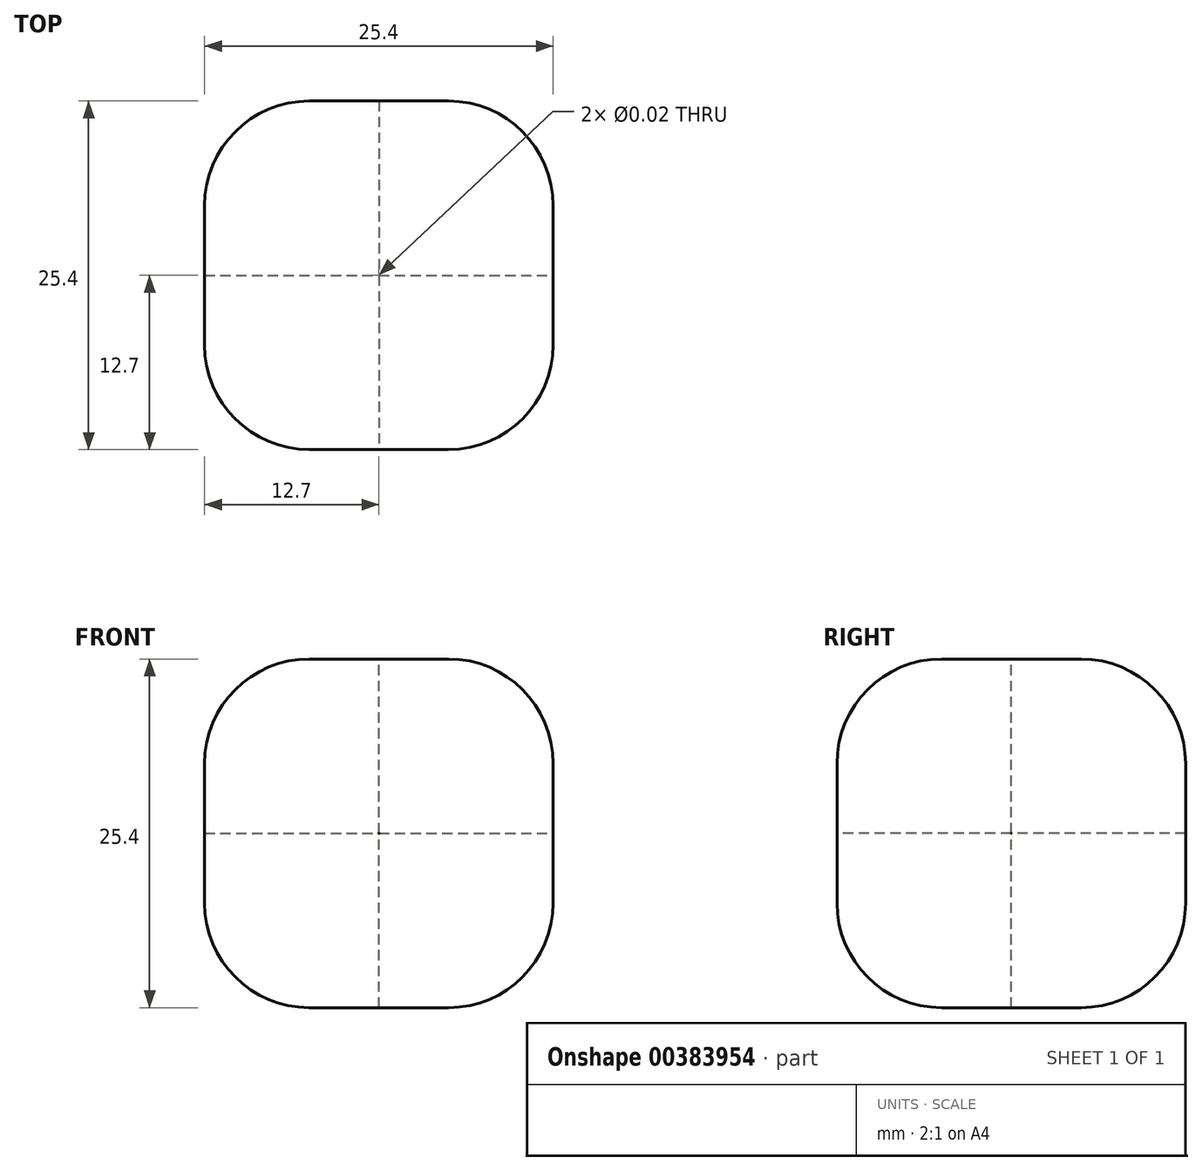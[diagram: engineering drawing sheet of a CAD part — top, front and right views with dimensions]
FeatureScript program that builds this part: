
annotation { "Feature Type Name" : "Feature", "Feature Type Description" : "" }
export const myFeature = defineFeature(function(context is Context, id is Id, definition is map)
    precondition{}
    {
        {
            var Q0;
            Q0=qCreatedBy(makeId("Front.planeOp"),FACE);
            var sketch = newSketch(context, id + "F0", { "sketchPlane" : qUnion([Q0])});
            skLineSegment(sketch, "E0.bottom", {"start": v(12.7, 12.7) * mm, "end": v(-12.7, 12.7) * mm});
            skLineSegment(sketch, "E0.top", {"start": v(12.7, -12.7) * mm, "end": v(-12.7, -12.7) * mm});
            skLineSegment(sketch, "E0.left", {"start": v(12.7, 12.7) * mm, "end": v(12.7, -12.7) * mm});
            skLineSegment(sketch, "E0.right", {"start": v(-12.7, 12.7) * mm, "end": v(-12.7, -12.7) * mm});
            skPoint(sketch, "E0.middle", {"position": v(0, 0) * mm});
            skSolve(sketch);
        }
        {
            var Q0;
            Q0 = qSketchRegion(id + "F0", true);
            extrude(context, id + "F1", {"entities" : qUnion([Q0]), "endBound" : BoundingType.SYMMETRIC, "depth" : 25.4 * mm});
        }
        {
            var Q0;
            Q0=makeQuery(id+"F1.opExtrude","SWEPT_FACE",FACE,{"disambiguationData":[OSD([sQuery(id+"F0.wireOp",EDGE,"E0.left")])]});
            var sketch = newSketch(context, id + "F2", { "sketchPlane" : qUnion([Q0])});
            skPoint(sketch, "E1", {"position": v(0, 0) * mm});
            skSolve(sketch);
        }
        {
            var Q0;
            Q0=makeQuery(id+"F1.opExtrude","CAP_FACE",FACE,{"disambiguationData":[OSD([sQuery(id+"F0.wireOp",EDGE,"E0.bottom"),sQuery(id+"F0.wireOp",EDGE,"E0.top"),sQuery(id+"F0.wireOp",EDGE,"E0.left"),sQuery(id+"F0.wireOp",EDGE,"E0.right")])],"isStart":false});
            var sketch = newSketch(context, id + "F3", { "sketchPlane" : qUnion([Q0])});
            skPoint(sketch, "E2", {"position": v(0, 0) * mm});
            skSolve(sketch);
        }
        {
            var Q0;
            Q0=makeQuery(id+"F1.opExtrude","SWEPT_FACE",FACE,{"disambiguationData":[OSD([sQuery(id+"F0.wireOp",EDGE,"E0.bottom")])]});
            var sketch = newSketch(context, id + "F4", { "sketchPlane" : qUnion([Q0])});
            skPoint(sketch, "E3", {"position": v(0, 0) * mm});
            skSolve(sketch);
        }
        {
            var Q0;
            Q0=sQuery(id+"F4.wireOp",VERTEX,"E3");
            var Q1;
            Q1=sQuery(id+"F3.wireOp",VERTEX,"E2");
            var Q2;
            Q2=sQuery(id+"F2.wireOp",VERTEX,"E1");
            var Q3;
            Q3=makeQuery(id+"F1.opExtrude","SWEPT_BODY",BODY,{"disambiguationData":[OSD([sQuery(id+"F0.wireOp",EDGE,"E0.bottom"),sQuery(id+"F0.wireOp",EDGE,"E0.top"),sQuery(id+"F0.wireOp",EDGE,"E0.left"),sQuery(id+"F0.wireOp",EDGE,"E0.right")])]});
            hole(context, id + "F5", {"style" : HoleStyle.SIMPLE, "endStyle" : HoleEndStyle.THROUGH, "standardTappedOrClearance" : lookupTablePath({ "standard" : "ANSI", "size" : "9/16 (0.56)", "type" : "Drilled" }), "standardBlindInLast" : lookupTablePath({ "standard" : "ANSI", "size" : "9/16", "type" : "Drilled" }), "holeDiameter" : 9 / 406.4 * mm, "isTappedThrough" : true, "tappedDepth" : 12.7 * mm, "tapClearance" : 3, "locations" : qUnion([Q0, Q1, Q2]), "scope" : qUnion([Q3])});
        }
        {
            var Q0;
            Q0=makeQuery(id+"F1.opExtrude","SWEPT_EDGE",EDGE,{"disambiguationData":[OSD([sQuery(id+"F0.wireOp",EDGE,"E0.bottom"),sQuery(id+"F0.wireOp",EDGE,"E0.left")])]});
            var Q1;
            Q1=makeQuery(id+"F1.opExtrude","SWEPT_EDGE",EDGE,{"disambiguationData":[OSD([sQuery(id+"F0.wireOp",EDGE,"E0.top"),sQuery(id+"F0.wireOp",EDGE,"E0.left")])]});
            var Q2;
            Q2=makeQuery(id+"F1.opExtrude","CAP_EDGE",EDGE,{"disambiguationData":[OSD([sQuery(id+"F0.wireOp",EDGE,"E0.left")])],"isStart":true});
            var Q3;
            Q3=makeQuery(id+"F1.opExtrude","CAP_EDGE",EDGE,{"disambiguationData":[OSD([sQuery(id+"F0.wireOp",EDGE,"E0.left")])],"isStart":false});
            var Q4;
            Q4=makeQuery(id+"F1.opExtrude","CAP_EDGE",EDGE,{"disambiguationData":[OSD([sQuery(id+"F0.wireOp",EDGE,"E0.bottom")])],"isStart":false});
            var Q5;
            Q5=makeQuery(id+"F1.opExtrude","CAP_EDGE",EDGE,{"disambiguationData":[OSD([sQuery(id+"F0.wireOp",EDGE,"E0.right")])],"isStart":false});
            var Q6;
            Q6=makeQuery(id+"F1.opExtrude","CAP_EDGE",EDGE,{"disambiguationData":[OSD([sQuery(id+"F0.wireOp",EDGE,"E0.top")])],"isStart":false});
            var Q7;
            Q7=makeQuery(id+"F1.opExtrude","SWEPT_EDGE",EDGE,{"disambiguationData":[OSD([sQuery(id+"F0.wireOp",EDGE,"E0.bottom"),sQuery(id+"F0.wireOp",EDGE,"E0.right")])]});
            var Q8;
            Q8=makeQuery(id+"F1.opExtrude","CAP_EDGE",EDGE,{"disambiguationData":[OSD([sQuery(id+"F0.wireOp",EDGE,"E0.bottom")])],"isStart":true});
            var Q9;
            Q9=makeQuery(id+"F1.opExtrude","SWEPT_EDGE",EDGE,{"disambiguationData":[OSD([sQuery(id+"F0.wireOp",EDGE,"E0.top"),sQuery(id+"F0.wireOp",EDGE,"E0.right")])]});
            var Q10;
            Q10=makeQuery(id+"F1.opExtrude","CAP_EDGE",EDGE,{"disambiguationData":[OSD([sQuery(id+"F0.wireOp",EDGE,"E0.right")])],"isStart":true});
            var Q11;
            Q11=makeQuery(id+"F1.opExtrude","CAP_EDGE",EDGE,{"disambiguationData":[OSD([sQuery(id+"F0.wireOp",EDGE,"E0.top")])],"isStart":true});
            fillet(context, id + "F6", {"entities" : qUnion([Q0, Q1, Q2, Q3, Q4, Q5, Q6, Q7, Q8, Q9, Q10, Q11]), "radius" : 7.62 * mm, "tangentPropagation" : true, "allowEdgeOverflow" : false});
        }
    });
